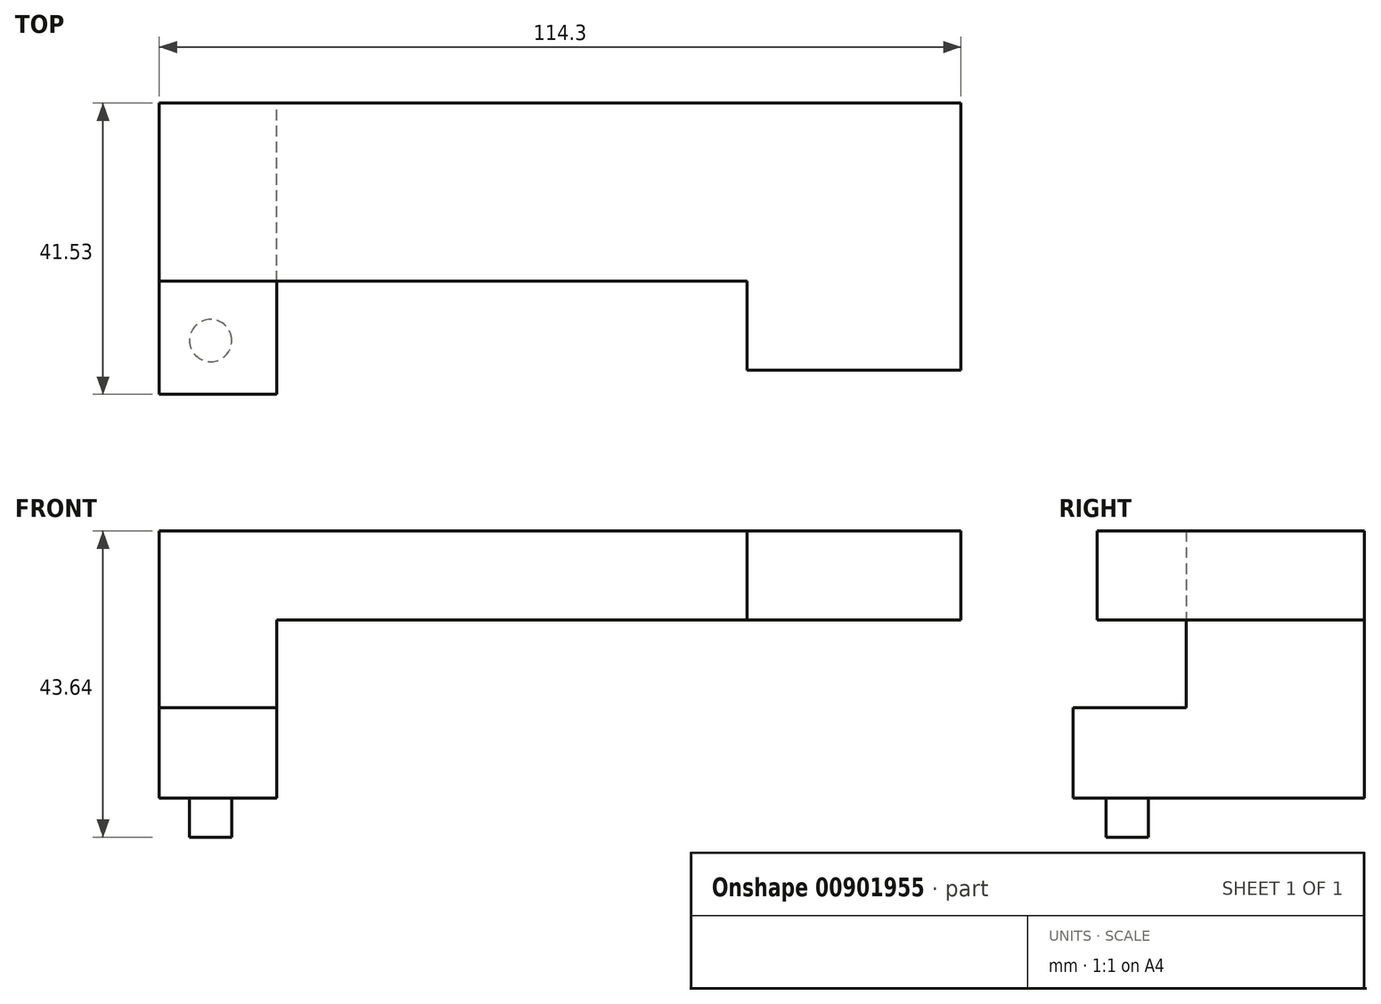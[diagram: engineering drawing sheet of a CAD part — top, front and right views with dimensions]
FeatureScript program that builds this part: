
annotation { "Feature Type Name" : "Feature", "Feature Type Description" : "" }
export const myFeature = defineFeature(function(context is Context, id is Id, definition is map)
    precondition{}
    {
        {
            var Q0;
            Q0=qCreatedBy(makeId("Front.planeOp"),FACE);
            var sketch = newSketch(context, id + "F0", { "sketchPlane" : qUnion([Q0])});
            skCircle(sketch, "E0", {"center": v(-27.09, 16.99) * mm, "radius": 25.4 * mm});
            skCircle(sketch, "E1", {"center": v(49.11, 16.99) * mm, "radius": 19.05 * mm});
            skLineSegment(sketch, "E2.bottom", {"start": v(-56.65, -27.73) * mm, "end": v(57.65, -27.73) * mm});
            skLineSegment(sketch, "E2.top", {"start": v(-56.65, -65.83) * mm, "end": v(57.65, -65.83) * mm});
            skLineSegment(sketch, "E2.left", {"start": v(-56.65, -27.73) * mm, "end": v(-56.65, -65.83) * mm});
            skLineSegment(sketch, "E2.right", {"start": v(57.65, -27.73) * mm, "end": v(57.65, -65.83) * mm});
            skLineSegment(sketch, "E3.bottom", {"start": v(-39.93, -40.43) * mm, "end": v(61.67, -40.43) * mm});
            skLineSegment(sketch, "E3.top", {"start": v(-39.93, -65.83) * mm, "end": v(61.67, -65.83) * mm});
            skLineSegment(sketch, "E3.left", {"start": v(-39.93, -40.43) * mm, "end": v(-39.93, -65.83) * mm});
            skLineSegment(sketch, "E3.right", {"start": v(61.67, -40.43) * mm, "end": v(61.67, -65.83) * mm});
            skSolve(sketch);
        }
        {
            var Q0;
            {var subQ1=sQuery(id+"F0.wireOp",EDGE,"E2.bottom");Q0=makeQuery(id+"F0.imprint","IMPRINT",FACE,{"disambiguationData":[TD([[makeQuery(id+"F0.imprint","IMPRINT",EDGE,{"derivedFrom":subQ1}),-1.0]])]});}
            extrude(context, id + "F1", {"entities" : qUnion([Q0]), "depth" : 25.4 * mm, "offsetDistance" : 25.4 * mm});
        }
        {
            var Q0;
            Q0=makeQuery(id+"F1.opExtrude","CAP_FACE",FACE,{"disambiguationData":[OSD([sQuery(id+"F0.wireOp",EDGE,"E2.bottom"),sQuery(id+"F0.wireOp",EDGE,"E2.top"),sQuery(id+"F0.wireOp",EDGE,"E2.left"),sQuery(id+"F0.wireOp",EDGE,"E2.right"),sQuery(id+"F0.wireOp",EDGE,"E3.bottom"),sQuery(id+"F0.wireOp",EDGE,"E3.left")])],"isStart":false});
            var sketch = newSketch(context, id + "F2", { "sketchPlane" : qUnion([Q0])});
            skLineSegment(sketch, "E4", {"start": v(-56.65, -52.93) * mm, "end": v(-39.93, -52.93) * mm});
            skPoint(sketch, "E4.endSnap0", {"position": v(-39.93, -53.13) * mm});
            skSolve(sketch);
        }
        {
            var Q0;
            {var subQ0=sQuery(id+"F2.wireOp",EDGE,"E4");Q0=makeQuery(id+"F2.imprint","IMPRINT",FACE,{"disambiguationData":[TD([[makeQuery(id+"F2.imprint","IMPRINT",EDGE,{"derivedFrom":subQ0}),-1.0]])]});}
            extrude(context, id + "F3", {"entities" : qUnion([Q0]), "operationType" : NewBodyOperationType.ADD, "depth" : 16.13 * mm, "offsetDistance" : 25.4 * mm});
        }
        {
            var Q0;
            Q0=makeQuery(id+"F3.opExtrude","SWEPT_FACE",FACE,{"disambiguationData":[OSD([sQuery(id+"F2.wireOp",EDGE,"E4")])]});
            var sketch = newSketch(context, id + "F4", { "sketchPlane" : qUnion([Q0])});
            skSolve(sketch);
        }
        {
            var Q0;
            Q0=makeQuery(id+"F1.opExtrude","CAP_FACE",FACE,{"disambiguationData":[OSD([sQuery(id+"F0.wireOp",EDGE,"E2.bottom"),sQuery(id+"F0.wireOp",EDGE,"E2.top"),sQuery(id+"F0.wireOp",EDGE,"E2.left"),sQuery(id+"F0.wireOp",EDGE,"E2.right"),sQuery(id+"F0.wireOp",EDGE,"E3.bottom"),sQuery(id+"F0.wireOp",EDGE,"E3.left")])],"isStart":false});
            var sketch = newSketch(context, id + "F5", { "sketchPlane" : qUnion([Q0])});
            skLineSegment(sketch, "E5", {"start": v(27.15, -27.73) * mm, "end": v(27.15, -40.43) * mm});
            skSolve(sketch);
        }
        {
            var Q0;
            {var subQ0=sQuery(id+"F5.wireOp",EDGE,"E5");Q0=makeQuery(id+"F5.imprint","IMPRINT",FACE,{"disambiguationData":[TD([[makeQuery(id+"F5.imprint","IMPRINT",EDGE,{"derivedFrom":subQ0}),1.0]])]});}
            extrude(context, id + "F6", {"entities" : qUnion([Q0]), "operationType" : NewBodyOperationType.ADD, "depth" : 12.7 * mm, "offsetDistance" : 25.4 * mm});
        }
        {
            var Q0;
            {var subQ0=sQuery(id+"F2.wireOp",EDGE,"E4");Q0=makeQuery(id+"F4.imprint","IMPRINT",FACE,{"disambiguationData":[TD([[makeQuery(id+"F4.imprint","IMPRINT",EDGE,{"derivedFrom":makeQuery(id+"F3.opExtrude","CAP_EDGE",EDGE,{"disambiguationData":[OSD([subQ0])],"isStart":false})}),1.0]])]});}
            var sketch = newSketch(context, id + "F7", { "sketchPlane" : qUnion([Q0])});
            skCircle(sketch, "E6", {"center": v(-49.32, -33.85) * mm, "radius": 3.02 * mm});
            skSolve(sketch);
        }
        {
            var Q0;
            Q0=makeQuery(id+"F7.imprint","IMPRINT",FACE,{"disambiguationData":[TD([[makeQuery(id+"F7.imprint","IMPRINT",EDGE,{"derivedFrom":sQuery(id+"F7.wireOp",EDGE,"E6")}),1.0]])]});
            extrude(context, id + "F8", {"entities" : qUnion([Q0]), "operationType" : NewBodyOperationType.ADD, "oppositeDirection" : true, "depth" : 18.44 * mm, "offsetDistance" : 25.4 * mm});
        }
    });
